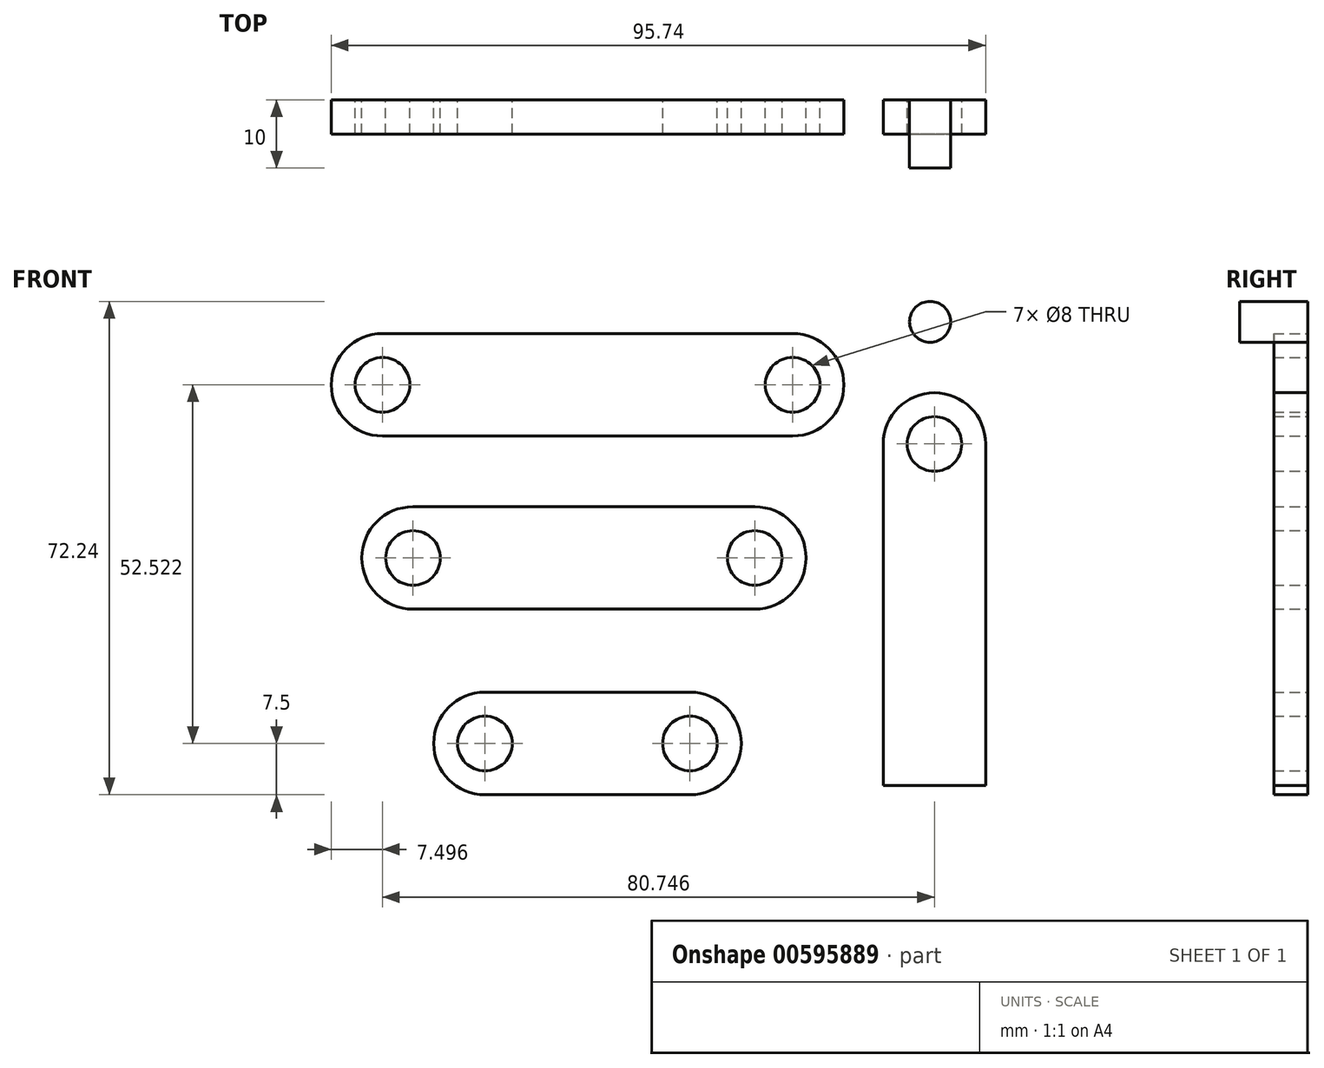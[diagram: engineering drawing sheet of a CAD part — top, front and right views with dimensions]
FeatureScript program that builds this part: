
annotation { "Feature Type Name" : "Feature", "Feature Type Description" : "" }
export const myFeature = defineFeature(function(context is Context, id is Id, definition is map)
    precondition{}
    {
        {
            assignVariable(context, id + "F0", {"name" : "thickness", "anyValue" : 5});
        }
        {
            var Q0;
            Q0=qCreatedBy(makeId("Front.planeOp"),FACE);
            var sketch = newSketch(context, id + "F1", { "sketchPlane" : qUnion([Q0])});
            skArc(sketch, "E0", {"start": v(0, 7.5) * mm, "mid": v(-7.5, 0) * mm, "end": v(0, -7.5) * mm});
            skArc(sketch, "E1", {"start": v(30, -7.5) * mm, "mid": v(37.5, 0) * mm, "end": v(30, 7.5) * mm});
            skLineSegment(sketch, "E2", {"start": v(0, 7.5) * mm, "end": v(30, 7.5) * mm});
            skLineSegment(sketch, "E3", {"start": v(0, -7.5) * mm, "end": v(30, -7.5) * mm});
            skCircle(sketch, "E4", {"center": v(0, 0) * mm, "radius": 4 * mm});
            skCircle(sketch, "E5", {"center": v(30, 0) * mm, "radius": 4 * mm});
            skSolve(sketch);
        }
        {
            var Q0;
            Q0=makeQuery(id+"F1.imprint","IMPRINT",FACE,{"disambiguationData":[TD([[makeQuery(id+"F1.imprint","IMPRINT",EDGE,{"derivedFrom":sQuery(id+"F1.wireOp",EDGE,"E0")}),1.0]])]});
            extrude(context, id + "F2", {"entities" : qUnion([Q0]), "depth" : (getVariable(context, 'thickness')) * mm, "offsetDistance" : 25.4 * mm});
        }
        {
            var Q0;
            Q0=qCreatedBy(makeId("Front.planeOp"),FACE);
            var sketch = newSketch(context, id + "F3", { "sketchPlane" : qUnion([Q0])});
            skArc(sketch, "E6", {"start": v(-10.52, 34.66) * mm, "mid": v(-18.02, 27.16) * mm, "end": v(-10.52, 19.66) * mm});
            skArc(sketch, "E7", {"start": v(39.48, 19.66) * mm, "mid": v(46.98, 27.16) * mm, "end": v(39.48, 34.66) * mm});
            skLineSegment(sketch, "E8", {"start": v(-10.52, 34.66) * mm, "end": v(39.48, 34.66) * mm});
            skLineSegment(sketch, "E9", {"start": v(-10.52, 19.66) * mm, "end": v(39.48, 19.66) * mm});
            skCircle(sketch, "E10", {"center": v(-10.52, 27.16) * mm, "radius": 4 * mm});
            skCircle(sketch, "E11", {"center": v(39.48, 27.16) * mm, "radius": 4 * mm});
            skSolve(sketch);
        }
        {
            var Q0;
            Q0 = qSketchRegion(id + "F3", true);
            extrude(context, id + "F4", {"entities" : qUnion([Q0]), "depth" : (getVariable(context, 'thickness')) * mm, "offsetDistance" : 25 * mm});
        }
        {
            var Q0;
            Q0=qCreatedBy(makeId("Front.planeOp"),FACE);
            var sketch = newSketch(context, id + "F5", { "sketchPlane" : qUnion([Q0])});
            skArc(sketch, "E12", {"start": v(-14.98, 60.02) * mm, "mid": v(-22.48, 52.52) * mm, "end": v(-14.98, 45.02) * mm});
            skArc(sketch, "E13", {"start": v(45.02, 45.02) * mm, "mid": v(52.52, 52.52) * mm, "end": v(45.02, 60.02) * mm});
            skLineSegment(sketch, "E14", {"start": v(-14.98, 60.02) * mm, "end": v(45.02, 60.02) * mm});
            skLineSegment(sketch, "E15", {"start": v(-14.98, 45.02) * mm, "end": v(45.02, 45.02) * mm});
            skCircle(sketch, "E16", {"center": v(-14.98, 52.52) * mm, "radius": 4 * mm});
            skCircle(sketch, "E17", {"center": v(45.02, 52.52) * mm, "radius": 4 * mm});
            skSolve(sketch);
        }
        {
            var Q0;
            Q0 = qSketchRegion(id + "F5", true);
            var Q1;
            Q1=sQuery(id+"F5.wireOp",EDGE,"E14");
            var Q2;
            Q2=sQuery(id+"F5.wireOp",EDGE,"E15");
            var Q3;
            Q3=sQuery(id+"F5.wireOp",EDGE,"E12");
            var Q4;
            Q4=sQuery(id+"F5.wireOp",EDGE,"E13");
            var Q5;
            Q5=sQuery(id+"F5.wireOp",EDGE,"E16");
            var Q6;
            Q6=sQuery(id+"F5.wireOp",EDGE,"E17");
            extrude(context, id + "F6", {"entities" : qUnion([Q0]), "surfaceEntities" : qUnion([Q1, Q2, Q3, Q4, Q5, Q6]), "depth" : (getVariable(context, 'thickness')) * mm, "offsetDistance" : 25 * mm});
        }
        {
            var Q0;
            Q0=qCreatedBy(makeId("Front.planeOp"),FACE);
            var sketch = newSketch(context, id + "F7", { "sketchPlane" : qUnion([Q0])});
            skLineSegment(sketch, "E18.top", {"start": v(58.26, -6.15) * mm, "end": v(73.26, -6.15) * mm});
            skLineSegment(sketch, "E18.left", {"start": v(58.26, 43.85) * mm, "end": v(58.26, -6.15) * mm});
            skLineSegment(sketch, "E18.right", {"start": v(73.26, 43.85) * mm, "end": v(73.26, -6.15) * mm});
            skArc(sketch, "E19", {"start": v(73.26, 43.85) * mm, "mid": v(65.76, 51.35) * mm, "end": v(58.26, 43.85) * mm});
            skCircle(sketch, "E20", {"center": v(65.76, 43.85) * mm, "radius": 4 * mm});
            skSolve(sketch);
        }
        {
            var Q0;
            Q0 = qSketchRegion(id + "F7", true);
            extrude(context, id + "F8", {"entities" : qUnion([Q0]), "depth" : (getVariable(context, 'thickness')) * mm, "offsetDistance" : 25 * mm});
        }
        {
            var Q0;
            Q0=qCreatedBy(makeId("Front.planeOp"),FACE);
            var sketch = newSketch(context, id + "F9", { "sketchPlane" : qUnion([Q0])});
            skCircle(sketch, "E21", {"center": v(65.13, 61.74) * mm, "radius": 3 * mm});
            skSolve(sketch);
        }
        {
            var Q0;
            Q0 = qSketchRegion(id + "F9", true);
            extrude(context, id + "F10", {"entities" : qUnion([Q0]), "depth" : (getVariable(context, 'thickness') * 2) * mm, "offsetDistance" : 25 * mm});
        }
    });
